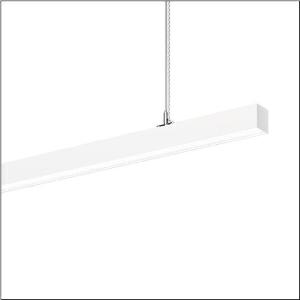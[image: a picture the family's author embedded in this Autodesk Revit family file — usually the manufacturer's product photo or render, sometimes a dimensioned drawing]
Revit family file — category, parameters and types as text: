
# Revit family: silica_r__21_51mx33db39wb_e509
name_source: partatom
category: Lighting Fixtures
units: mm (PartAtom-declared; Revit-internal decimal feet)

## family parameters
Cut with Voids When Loaded = No
Host = Face
Light Source = No
Part Type = Normal
Room Calculation Point = No
Round Connector Dimension = Use Diameter
Shared = No

## types (1)
- --- (1 x LED, 7390 lm, 51.6 W, 3000K)
    Apparent Load = 52 VA
    CIE Flux Codes = 78 96 99 55 100
    Color Rendering = 80
    Color Temperature = 3000K
    Default Elevation = 1800 mm
    Description = Silica® 21, office luminaire, primary optical cover: prismatic diffuser, of PMMA, CAT 2 (L<= 3000cd/m²), light emission: direct/indirect distribution, primary light characteristic: symmetric, installation type: suspended mounting, LED, rated luminous flux: 7.390lm, luminous efficacy: 143lm/W, light colour: 830, colour temperature: 3000K, with terminal, 3+2-pole, max. 2.5mm², mains connection: 220..240V, AC, 50/60Hz, rated input power: 51.6W, luminaire housing, of aluminium, traffic white (RAL 9016), length: 1.504mm, width: 53mm, height: 53mm, protection rating (complete): IP20, insulation class (complete): insulation class I (protective earthing), certification: CE, permissible operating ambient temperature: 0..+35°C, standard: EN 50419, packaging unit: 1 piece
    Height = 53 mm
    Lamp = 1 x LED
    Lamp Light Flux = 7390 lm
    Lamp Power = 51.6 W
    Lamp count = 1
    Length = 1504 mm
    Luminous efficacy = 143 lm/W
    Manufacturer = Siteco
    ModVariant = No
    Model = 51MX33DB39WB
    Mounting Place = Ceiling
    Mounting Type = Pendant
    Number of Poles = 1
    OnlyDefault = Yes
    Power Factor = 1
    Product Name = Silica® 21
    Product group = office luminaire | ceiling pendant
    ProductGroupID = 902
    Protection Class = Protection class I
    Protection Degree = IP 20
    RLX_Detail_Level = 1
    RLX_Emergency_Light_Flux = 0 lm
    RLX_Emergency_Type = 0
    RLX_Emergency_Type_DB = No
    RlxData = <blob elided: 21421 chars, md5=ac12de3b>
    Socket = socket
    Standby Power = 0 W
    System Light Flux = 7390 lm
    System Power = 52 W
    Type Comments = factory setting: luminous flux: 100 % | dim-lin: 254 | 345 mA
    Type Image = l_1335916.jpg
    URL = http://relux.com
    VarID = @adj_087419
    Voltage = 0 V
    Weight = 0.00 kg
    Width = 53 mm

## geometry (parser evidence)
native form markers: Blend x4, Sweep x12
no freeform markers — native parametric forms only
